# Revit family: BE_84456_de_DE
name_source: partatom
category: Leuchten
revit_build: Autodesk Revit 2017 (Build: 20160225_1515(x64)
units: mm (PartAtom-declared; Revit-internal decimal feet)

## family parameters
Basisbauteil = Fläche
Beim Laden mit Abzugskörper schneiden = Ja
Bemaßung runder Anschluss = Durchmesser verwenden
Gemeinsam genutzt = Nein
Lichtquelle = Ja
Raumberechnungspunkt = Ja
Teiletyp = Normal

## types (6) — shared parameters
AC/DC = AC/DC
Aktualisierung = 2022-05-12T04:00:08
Anschlussleitung = 1.8 m 07RN8-F 5 G 1²
Beschreibung = Bodeneinbauleuchte
Beschreibung_Sonderanfertigung = Hier können Sie Informationen zur Sonderanfertigung eintragen.
CE_Konformität = ja
ENEC = ja
Einbau_in_Wärmedämmung = ungeeignet
Einbaugehäuse = Nein
Energieeffizienzklasse = LED A++ - A
Farbfilter = 16777215
Farbtemperaturverschiebung bei Dämpfen der Lampe = <Keine Auswahl>
Farbwiedergabeindex = CRI > 80
Frequenz = 0/50-60 Hz
Gewicht = 7.3 kg
Hersteller = BEGA
Lampe = LED 28.1 W
Lastklassifizierung = Beleuchtung
Lebensdauerkriterien = L70B50 @ 25 °C = 64000 h
Logo = BEGA_Logo.png
Material_03 = BEGA_Oberfläche_Weiss_matt
Material_04 = BEGA_Kunststoff_Grafit_matt
Material_06 = BEGA_Oberfläche_Edelstahl_gebürstet
Material_09 = BEGA_Glas_klar
Material_13 = BEGA_Kunststoff_matt
Material_15 = BEGA_Leuchtmedium_matt
Material_17 = BEGA_Reflektor
Material_18 = BEGA_Gummi_schwarz
Neigungswinkel = 0.00°
Oberflächentemperatur = 35 °C
Produktdatenblatt = https://cdn.bega.com
Scheinlast = 0 VA
Schutzart = IP 68...10m
Schutzklasse = I
Sonderanfertigung = Nein
Spannung = 240 V
Typenbild = 84456.png
URL = https://www.bega.com
Umgebungstemperatur = 25 °C
zero-valued in all types: Vorgabe-Ansicht

## per-type parameters (varying)
| type | Bestellnummer | Datei für fotometrisches Netz | Farbtemperatur | LED_Modulbezeichnung | Lampenlichtstrom | Leuchtenlichtstrom | Modell | Rutschhemmendes_Glas |
| BEGA_84456_K27 | 84456K27 | BE_84456K27.IES | 2700 K | LED-1004/827 | 4720 lm | 3199 lm | 84456K27 |  |
| BEGA_84456_K3 | 84456K3 | BE_84456K3.IES | 3000 K | LED-1004/830 | 4895 lm | 3318 lm | 84456K3 |  |
| BEGA_84456_K4 | 84456K4 | BE_84456K4.IES | 4000 K | LED-1004/840 | 4965 lm | 3365 lm | 84456K4 |  |
| BEGA_84456_R_K4 | 84456RK4 | BE_84456RK4.IES | 4000 K | LED-1004/840 | 4965 lm | 3365 lm | 84456RK4 | ja |
| BEGA_84456_R_K3 | 84456RK3 | BE_84456RK3.IES | 3000 K | LED-1004/830 | 4895 lm | 3318 lm | 84456RK3 | ja |
| BEGA_84456_R_K27 | 84456RK27 | BE_84456RK27.IES | 2700 K | LED-1004/827 | 4720 lm | 3199 lm | 84456RK27 | ja |
